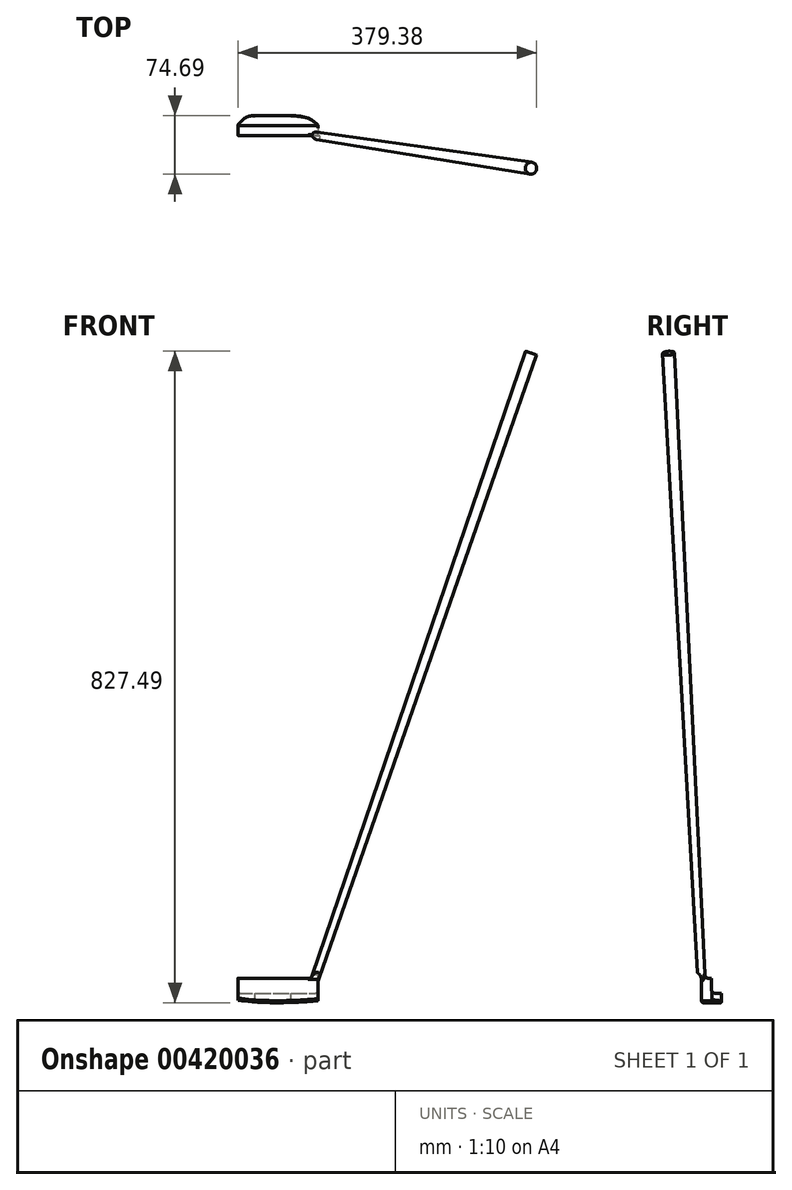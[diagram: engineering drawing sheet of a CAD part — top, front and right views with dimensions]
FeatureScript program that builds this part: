
annotation { "Feature Type Name" : "Feature", "Feature Type Description" : "" }
export const myFeature = defineFeature(function(context is Context, id is Id, definition is map)
    precondition{}
    {
        {
            var Q0;
            Q0=qCreatedBy(makeId("Front.planeOp"),FACE);
            var sketch = newSketch(context, id + "F0", { "sketchPlane" : qUnion([Q0])});
            skLineSegment(sketch, "E0.top", {"start": v(0, 31.75) * mm, "end": v(101.6, 31.75) * mm});
            skLineSegment(sketch, "E0.left", {"start": v(0, 4.05) * mm, "end": v(0, 31.75) * mm});
            skLineSegment(sketch, "E0.right", {"start": v(101.6, 3.3) * mm, "end": v(101.6, 31.75) * mm});
            skPoint(sketch, "E1", {"position": v(50.8, 0) * mm});
            skLineSegment(sketch, "E2", {"start": v(101.6, 3.3) * mm, "end": v(101.6, 889) * mm, "construction": true});
            skLineSegment(sketch, "E3", {"start": v(50.8, 0) * mm, "end": v(339.76, 839.2) * mm, "construction": true});
            skFitSpline(sketch, "E4", {"points": [v(0, 4.05) * mm, v(101.6, 3.3) * mm], "startDerivative": vector(86.22, -12.36) * mm, "endDerivative": vector(116.02, 10.14) * mm});
            skPoint(sketch, "E5.orphan", {"position": v(0, 0) * mm});
            skPoint(sketch, "E6.orphan", {"position": v(101.6, 0) * mm});
            skSolve(sketch);
        }
        {
            var Q0;
            Q0 = qSketchRegion(id + "F0", true);
            extrude(context, id + "F1", {"entities" : qUnion([Q0]), "oppositeDirection" : true, "depth" : 25.4 * mm});
        }
        {
            var Q0;
            Q0=makeQuery(id+"F1.opExtrude","SWEPT_FACE",FACE,{"disambiguationData":[OSD([sQuery(id+"F0.wireOp",EDGE,"E0.right")])]});
            var sketch = newSketch(context, id + "F2", { "sketchPlane" : qUnion([Q0])});
            skLineSegment(sketch, "E7", {"start": v(0, 31.75) * mm, "end": v(12.7, 31.75) * mm, "construction": true});
            skPoint(sketch, "E8.endSnap0", {"position": v(25.4, 17.53) * mm});
            skLineSegment(sketch, "E9", {"start": v(12.7, 31.75) * mm, "end": v(12.7, 12.7) * mm});
            skLineSegment(sketch, "E10", {"start": v(12.7, 12.7) * mm, "end": v(25.4, 12.7) * mm});
            skLineSegment(sketch, "E11", {"start": v(12.7, 31.75) * mm, "end": v(25.4, 31.75) * mm});
            skLineSegment(sketch, "E12", {"start": v(25.4, 31.75) * mm, "end": v(25.4, 12.7) * mm});
            skSolve(sketch);
        }
        {
            var Q0;
            Q0=makeQuery(id+"F2.imprint","IMPRINT",FACE,{"disambiguationData":[TD([[makeQuery(id+"F2.imprint","IMPRINT",EDGE,{"derivedFrom":sQuery(id+"F2.wireOp",EDGE,"4f6f9453-9990-41ff-83f2-817189d57def")}),1.0]])]});
            var Q1;
            Q1=makeQuery(id+"F2.imprint","IMPRINT",FACE,{"disambiguationData":[TD([[makeQuery(id+"F2.imprint","IMPRINT",EDGE,{"derivedFrom":sQuery(id+"F2.wireOp",EDGE,"E9")}),1.0]])]});
            extrude(context, id + "F3", {"entities" : qUnion([Q0, Q1]), "operationType" : NewBodyOperationType.REMOVE, "oppositeDirection" : true, "depth" : 108.7 * mm});
        }
        {
            var Q0;
            Q0=makeQuery(id+"F3.boolean.opBoolean","COPY",FACE,{"derivedFrom":makeQuery(id+"F3.opExtrude","SWEPT_FACE",FACE,{"disambiguationData":[OSD([sQuery(id+"F2.wireOp",EDGE,"E10")])]})});
            cPlane(context, id + "F4", {"entities" : qUnion([Q0]), "cplaneType" : CPlaneType.OFFSET, "offset" : 0 * mm, "width" : 152.4 * mm, "height" : 152.4 * mm});
        }
        {
            var Q0;
            Q0=qCreatedBy(id+"F4.planeOp",FACE);
            var sketch = newSketch(context, id + "F5", { "sketchPlane" : qUnion([Q0])});
            skLineSegment(sketch, "E13", {"start": v(0, 0) * mm, "end": v(0, 26.94) * mm, "construction": true});
            skLineSegment(sketch, "E14", {"start": v(0, 26.94) * mm, "end": v(0, 25.4) * mm, "construction": true});
            skLineSegment(sketch, "E15", {"start": v(0, 25.4) * mm, "end": v(101.6, 25.4) * mm, "construction": true});
            skLineSegment(sketch, "E16", {"start": v(101.6, 25.4) * mm, "end": v(101.6, -3.33) * mm, "construction": true});
            skFitSpline(sketch, "E17", {"points": [v(0, 13.47) * mm, v(9.64, 22.6) * mm, v(21.39, 25.4) * mm], "startDerivative": vector(17.5, 20.93) * mm, "endDerivative": vector(25.33, 2.79) * mm});
            skFitSpline(sketch, "E18", {"points": [v(67.14, 25.4) * mm, v(90.32, 21.38) * mm, v(101.6, 13.14) * mm], "startDerivative": vector(45.31, -3.79) * mm, "endDerivative": vector(22.64, -21.5) * mm});
            skLineSegment(sketch, "E19", {"start": v(0, 13.47) * mm, "end": v(0, 25.4) * mm});
            skLineSegment(sketch, "E20", {"start": v(67.14, 25.4) * mm, "end": v(101.6, 25.4) * mm});
            skLineSegment(sketch, "E21", {"start": v(0, 25.4) * mm, "end": v(21.39, 25.4) * mm});
            skLineSegment(sketch, "E22", {"start": v(101.6, 25.4) * mm, "end": v(101.6, 13.14) * mm});
            skSolve(sketch);
        }
        {
            var Q0;
            Q0=makeQuery(id+"F5.imprint","IMPRINT",FACE,{"disambiguationData":[TD([[makeQuery(id+"F5.imprint","IMPRINT",EDGE,{"derivedFrom":sQuery(id+"F5.wireOp",EDGE,"E17")}),1.0]])]});
            var Q1;
            Q1=makeQuery(id+"F5.imprint","IMPRINT",FACE,{"disambiguationData":[TD([[makeQuery(id+"F5.imprint","IMPRINT",EDGE,{"derivedFrom":sQuery(id+"F5.wireOp",EDGE,"E18")}),1.0]])]});
            extrude(context, id + "F6", {"entities" : qUnion([Q0, Q1]), "operationType" : NewBodyOperationType.REMOVE, "oppositeDirection" : true, "depth" : 25.4 * mm});
        }
        {
            var Q0;
            Q0=makeQuery(id+"F3.boolean.opBoolean","COPY",EDGE,{"derivedFrom":makeQuery(id+"F3.opExtrude","SWEPT_EDGE",EDGE,{"disambiguationData":[OSD([sQuery(id+"F2.wireOp",EDGE,"E9"),sQuery(id+"F2.wireOp",EDGE,"E10")])]})});
            var Q1;
            Q1=makeQuery(id+"F3.boolean.opBoolean","COPY",EDGE,{"derivedFrom":makeQuery(id+"F3.opExtrude","SWEPT_EDGE",EDGE,{"disambiguationData":[OSD([sQuery(id+"F0.wireOp",EDGE,"E0.top"),sQuery(id+"F0.wireOp",EDGE,"E0.right"),sQuery(id+"F2.wireOp",EDGE,"E9"),sQuery(id+"F2.wireOp",EDGE,"E11")])]})});
            fillet(context, id + "F7", {"entities" : qUnion([Q0, Q1]), "radius" : 5.08 * mm, "tangentPropagation" : true, "allowEdgeOverflow" : false});
        }
        {
            var Q0;
            Q0=makeQuery(id+"F6.boolean.opBoolean","COPY",EDGE,{"derivedFrom":makeQuery(id+"F6.opExtrude","CAP_EDGE",EDGE,{"disambiguationData":[OSD([sQuery(id+"F5.wireOp",EDGE,"E18")])],"isStart":true})});
            var Q1;
            Q1=makeQuery(id+"F3.boolean.opBoolean","COPY",EDGE,{"derivedFrom":makeQuery(id+"F3.opExtrude","SWEPT_EDGE",EDGE,{"disambiguationData":[OSD([sQuery(id+"F0.wireOp",EDGE,"E0.right"),sQuery(id+"F2.wireOp",EDGE,"E10"),sQuery(id+"F2.wireOp",EDGE,"E12")])]})});
            var Q2;
            Q2=makeQuery(id+"F6.boolean.opBoolean","COPY",EDGE,{"derivedFrom":makeQuery(id+"F6.opExtrude","CAP_EDGE",EDGE,{"disambiguationData":[OSD([sQuery(id+"F5.wireOp",EDGE,"E17")])],"isStart":true})});
            var Q3;
            Q3=makeQuery(id+"F1.opExtrude","CAP_EDGE",EDGE,{"disambiguationData":[OSD([sQuery(id+"F0.wireOp",EDGE,"E4")])],"isStart":false});
            var Q4;
            Q4=makeQuery(id+"F6.boolean.opBoolean","INTERSECT",EDGE,{"derivedFrom":[makeQuery(id+"F1.opExtrude","SWEPT_FACE",FACE,{"disambiguationData":[OSD([sQuery(id+"F0.wireOp",EDGE,"E4")])]}),makeQuery(id+"F6.opExtrude","SWEPT_FACE",FACE,{"disambiguationData":[OSD([sQuery(id+"F5.wireOp",EDGE,"E18")])]})]});
            var Q5;
            Q5=makeQuery(id+"F6.boolean.opBoolean","INTERSECT",EDGE,{"derivedFrom":[makeQuery(id+"F1.opExtrude","SWEPT_FACE",FACE,{"disambiguationData":[OSD([sQuery(id+"F0.wireOp",EDGE,"E4")])]}),makeQuery(id+"F6.opExtrude","SWEPT_FACE",FACE,{"disambiguationData":[OSD([sQuery(id+"F5.wireOp",EDGE,"E17")])]})]});
            var Q6;
            Q6=makeQuery(id+"F3.boolean.opBoolean","INTERSECT",EDGE,{"derivedFrom":[makeQuery(id+"F1.opExtrude","SWEPT_FACE",FACE,{"disambiguationData":[OSD([sQuery(id+"F0.wireOp",EDGE,"E0.left")])]}),makeQuery(id+"F3.opExtrude","SWEPT_FACE",FACE,{"disambiguationData":[OSD([sQuery(id+"F2.wireOp",EDGE,"E9")])]})]});
            var Q7;
            Q7=makeQuery(id+"F3.boolean.opBoolean","COPY",EDGE,{"derivedFrom":makeQuery(id+"F3.opExtrude","CAP_EDGE",EDGE,{"disambiguationData":[OSD([sQuery(id+"F2.wireOp",EDGE,"E9")])],"isStart":true})});
            fillet(context, id + "F8", {"entities" : qUnion([Q0, Q1, Q2, Q3, Q4, Q5, Q6, Q7]), "radius" : 1.27 * mm, "tangentPropagation" : true, "allowEdgeOverflow" : false});
        }
        {
            var Q0;
            Q0=makeQuery(id+"F1.opExtrude","CAP_EDGE",EDGE,{"disambiguationData":[OSD([sQuery(id+"F0.wireOp",EDGE,"E4")])],"isStart":true});
            fillet(context, id + "F9", {"entities" : qUnion([Q0]), "radius" : 2.54 * mm, "tangentPropagation" : true, "allowEdgeOverflow" : false});
        }
        {
            var Q0;
            Q0=makeQuery(id+"F1.opExtrude","CAP_EDGE",EDGE,{"disambiguationData":[OSD([sQuery(id+"F0.wireOp",EDGE,"E0.top")])],"isStart":true});
            fillet(context, id + "F10", {"entities" : qUnion([Q0]), "radius" : 1.27 * mm, "tangentPropagation" : true, "allowEdgeOverflow" : false});
        }
        {
            var Q0;
            Q0=qCreatedBy(makeId("Front.planeOp"),FACE);
            var sketch = newSketch(context, id + "F11", { "sketchPlane" : qUnion([Q0])});
            skLineSegment(sketch, "E23.top", {"start": v(0, 31.75) * mm, "end": v(101.6, 31.75) * mm});
            skLineSegment(sketch, "E23.left", {"start": v(0, 4.05) * mm, "end": v(0, 31.75) * mm});
            skLineSegment(sketch, "E23.right", {"start": v(101.6, 3.3) * mm, "end": v(101.6, 31.75) * mm});
            skPoint(sketch, "E24", {"position": v(50.8, 0) * mm});
            skLineSegment(sketch, "E25", {"start": v(101.6, 3.3) * mm, "end": v(101.6, 889) * mm, "construction": true});
            skLineSegment(sketch, "E26", {"start": v(50.8, 0) * mm, "end": v(339.76, 839.2) * mm, "construction": true});
            skFitSpline(sketch, "E27", {"points": [v(0, 4.05) * mm, v(101.6, 3.3) * mm], "startDerivative": vector(86.22, -12.36) * mm, "endDerivative": vector(116.02, 10.14) * mm});
            skPoint(sketch, "E28.orphan", {"position": v(0, 0) * mm});
            skPoint(sketch, "E29.orphan", {"position": v(101.6, 0) * mm});
            skLineSegment(sketch, "E30.0", {"start": v(83.22, -11.16) * mm, "end": v(372.18, 828.03) * mm, "construction": true});
            skSolve(sketch);
        }
        {
            var Q0;
            Q0=qCreatedBy(makeId("Front.planeOp"),FACE);
            var Q1;
            {var subQ0=sQuery(id+"F0.wireOp",EDGE,"E0.top");Q1=makeQuery(id+"F10.opFillet","BLEND_EDGE",EDGE,{"blendedFrom":[makeQuery(id+"F1.opExtrude","CAP_EDGE",EDGE,{"disambiguationData":[OSD([subQ0])],"isStart":true}),makeQuery(id+"F1.opExtrude","CAP_FACE",FACE,{"disambiguationData":[OSD([subQ0,sQuery(id+"F0.wireOp",EDGE,"E0.left"),sQuery(id+"F0.wireOp",EDGE,"E0.right"),sQuery(id+"F0.wireOp",EDGE,"E4")])],"isStart":true})],"blendedInto":[makeQuery(id+"F1.opExtrude","CAP_FACE",FACE,{"disambiguationData":[OSD([subQ0,sQuery(id+"F0.wireOp",EDGE,"E0.left"),sQuery(id+"F0.wireOp",EDGE,"E0.right"),sQuery(id+"F0.wireOp",EDGE,"E4")])],"isStart":true})]});}
            cPlane(context, id + "F12", {"entities" : qUnion([Q0, Q1]), "cplaneType" : CPlaneType.LINE_ANGLE, "offset" : 25.4 * mm, "angle" : 3 * degree, "width" : 152.4 * mm, "height" : 152.4 * mm});
        }
        {
            var Q0;
            Q0=qCreatedBy(id+"F12.planeOp",FACE);
            var sketch = newSketch(context, id + "F13", { "sketchPlane" : qUnion([Q0])});
            skLineSegment(sketch, "E31.0", {"start": v(-83.22, -11.15) * mm, "end": v(-372.18, 826.9) * mm});
            skSolve(sketch);
        }
        {
            var Q0;
            Q0=sQuery(id+"F13.wireOp",EDGE,"E31.0");
            var Q1;
            Q1=sQuery(id+"F13.wireOp",VERTEX,"E31.0.end");
            cPlane(context, id + "F14", {"entities" : qUnion([Q0, Q1]), "cplaneType" : CPlaneType.LINE_POINT, "offset" : 25.4 * mm, "width" : 152.4 * mm, "height" : 152.4 * mm});
        }
        {
            var Q0;
            Q0=qCreatedBy(id+"F14.planeOp",FACE);
            var sketch = newSketch(context, id + "F15", { "sketchPlane" : qUnion([Q0])});
            skPoint(sketch, "E32.0", {"position": v(82.31, 1.6) * mm});
            skCircle(sketch, "E33", {"center": v(82.31, 1.6) * mm, "radius": 7.62 * mm});
            skSolve(sketch);
        }
        {
            var Q0;
            Q0=qCreatedBy(id+"F14.planeOp",FACE);
            cPlane(context, id + "F16", {"entities" : qUnion([Q0]), "cplaneType" : CPlaneType.OFFSET, "offset" : 850.9 * mm, "oppositeDirection" : true, "width" : 152.4 * mm, "height" : 152.4 * mm});
        }
        {
            var Q0;
            Q0=qCreatedBy(id+"F16.planeOp",FACE);
            var sketch = newSketch(context, id + "F17", { "sketchPlane" : qUnion([Q0])});
            skPoint(sketch, "E34.0", {"position": v(82.31, 1.6) * mm});
            skCircle(sketch, "E35", {"center": v(82.31, 1.6) * mm, "radius": 4.7 * mm});
            skSolve(sketch);
        }
        {
            var Q1;
            Q1=makeQuery(id+"F15.imprint","IMPRINT",FACE,{"disambiguationData":[TD([[makeQuery(id+"F15.imprint","IMPRINT",EDGE,{"derivedFrom":sQuery(id+"F15.wireOp",EDGE,"E33")}),1.0]])]});
            var Q2;
            Q2=makeQuery(id+"F17.imprint","IMPRINT",FACE,{"disambiguationData":[TD([[makeQuery(id+"F17.imprint","IMPRINT",EDGE,{"derivedFrom":sQuery(id+"F17.wireOp",EDGE,"E35")}),1.0]])]});
            loft(context, id + "F18", {"operationType" : NewBodyOperationType.ADD, "sheetProfilesArray" : [{ "sheetProfileEntities" : qUnion([Q1]) }, { "sheetProfileEntities" : qUnion([Q2]) }]});
        }
        {
            var Q0;
            Q0=qCreatedBy(makeId("Right.planeOp"),FACE);
            var sketch = newSketch(context, id + "F19", { "sketchPlane" : qUnion([Q0])});
            skLineSegment(sketch, "E36.0", {"start": v(0, 3.3) * mm, "end": v(0, 30.48) * mm});
            skPoint(sketch, "E37.0", {"position": v(0, 30.48) * mm});
            skPoint(sketch, "E38.orphan", {"position": v(0, 31.75) * mm});
            skLineSegment(sketch, "E39", {"start": v(-4.28, 22.27) * mm, "end": v(-49.3, 825.44) * mm});
            skFitSpline(sketch, "E40", {"points": [v(0, 30.48) * mm, v(-1.4, 35.04) * mm, v(-5.23, 39.27) * mm], "startDerivative": vector(-1.89, 9.89) * mm, "endDerivative": vector(-8.47, 7.72) * mm});
            skLineSegment(sketch, "E41", {"start": v(-4.28, 22.27) * mm, "end": v(-8.18, 17.9) * mm});
            skLineSegment(sketch, "E42", {"start": v(-8.18, 17.9) * mm, "end": v(0, 3.3) * mm});
            skSolve(sketch);
        }
        {
            var Q0;
            Q0=makeQuery(id+"F19.imprint","IMPRINT",FACE,{"disambiguationData":[TD([[makeQuery(id+"F19.imprint","IMPRINT",EDGE,{"derivedFrom":sQuery(id+"F19.wireOp",EDGE,"E36.0")}),1.0]])]});
            extrude(context, id + "F20", {"entities" : qUnion([Q0]), "operationType" : NewBodyOperationType.REMOVE, "depth" : 193.55 * mm});
        }
        {
            var Q0;
            Q0=makeQuery(id+"F18.boolean.opBoolean","INTERSECT",EDGE,{"derivedFrom":[makeQuery(id+"F1.opExtrude","SWEPT_FACE",FACE,{"disambiguationData":[OSD([sQuery(id+"F0.wireOp",EDGE,"E0.top")])]}),makeQuery(id+"F18.opLoft","SWEPT_FACE",FACE,{"disambiguationData":[OSD([sQuery(id+"F15.wireOp",EDGE,"E33"),sQuery(id+"F17.wireOp",EDGE,"E35")])]})]});
            fillet(context, id + "F21", {"entities" : qUnion([Q0]), "radius" : 5.08 * mm, "tangentPropagation" : true, "allowEdgeOverflow" : false});
        }
    });
